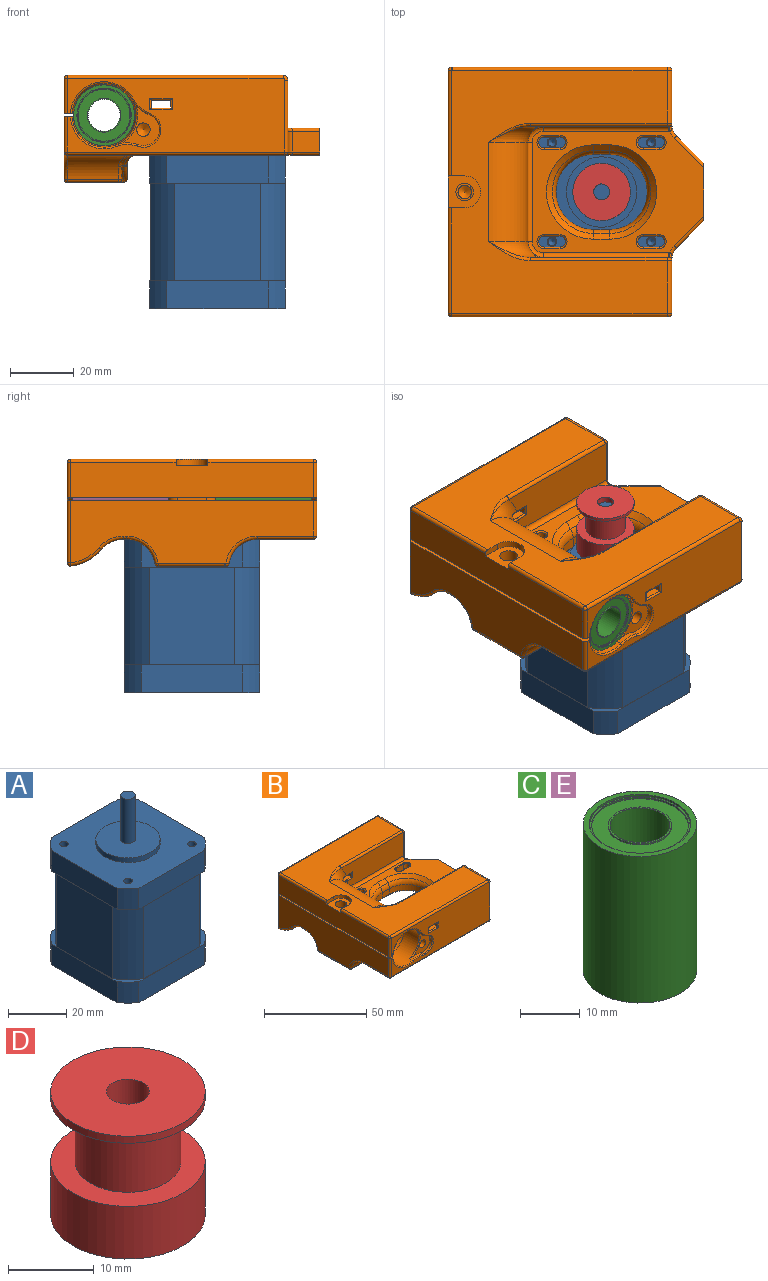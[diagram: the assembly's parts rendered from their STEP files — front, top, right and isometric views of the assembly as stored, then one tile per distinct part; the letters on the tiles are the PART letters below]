
ASSEMBLY  parts=5 mates=1
PART A: 48 faces, bbox 42.4x42.4x68.5 mm
  f0: cylinder r=1.5mm len=6mm, axis (0,0,1), area 56.5mm2, adj f18,f26
  f1: cylinder r=1.25mm len=2.5mm, axis (0,0,1), area 11.8mm2, adj f2,f26
  f2: cone r=1.25mm half-angle=59deg, axis (0,0,1), area 5.7mm2, adj f1
  f3: cylinder r=1.5mm len=6mm, axis (0,0,1), area 56.5mm2, adj f18,f25
  f4: cylinder r=1.25mm len=2.5mm, axis (0,0,1), area 11.8mm2, adj f5,f25
  f5: cone r=1.25mm half-angle=59deg, axis (0,0,1), area 5.7mm2, adj f4
  f6: cylinder r=1.5mm len=6mm, axis (0,0,1), area 56.5mm2, adj f18,f24
  f7: cylinder r=1.25mm len=2.5mm, axis (0,0,1), area 11.8mm2, adj f8,f24
  f8: cone r=1.25mm half-angle=59deg, axis (0,0,1), area 5.7mm2, adj f7
  f9: cylinder r=1.5mm len=6mm, axis (0,0,1), area 56.5mm2, adj f18,f23
  f10: cylinder r=1.25mm len=2.5mm, axis (0,0,1), area 11.8mm2, adj f11,f23
  f11: cone r=1.25mm half-angle=59deg, axis (0,0,1), area 5.7mm2, adj f10
  f12: cylinder r=11mm len=22mm, axis (0,0,-1), area 138.2mm2, adj f13,f18
  f13: plane 22x22mm, normal (0,0,1), area 360.5mm2, adj f12,f46
  f14: plane 31.78x8.75mm, normal (1,0,0), area 278mm2, adj f18,f19,f20,f28
  f15: plane 31.78x8.75mm, normal (0,-1,0), area 278mm2, adj f18,f19,f21,f28
  f16: plane 31.78x8.75mm, normal (-1,0,0), area 278mm2, adj f18,f21,f22,f28
  f17: plane 31.78x8.75mm, normal (0,1,0), area 278mm2, adj f18,f20,f22,f28
  f18: plane 42.42x42.42mm, normal (0,0,1), area 1339.6mm2, adj f0,f3,f6,f9,f12,f14,f15,f16
  f19: cylinder r=26.5mm len=8.75mm, axis (0,0,-1), area 66.1mm2, adj f14,f15,f18,f28
  f20: cylinder r=26.5mm len=8.75mm, axis (0,0,-1), area 66.1mm2, adj f14,f17,f18,f28
  f21: cylinder r=26.5mm len=8.75mm, axis (0,0,-1), area 66.1mm2, adj f15,f16,f18,f28
  f22: cylinder r=26.5mm len=8.75mm, axis (0,0,-1), area 66.1mm2, adj f16,f17,f18,f28
  f23: plane 3x3mm, normal (0,0,1), area 2.2mm2, adj f9,f10
  f24: plane 3x3mm, normal (0,0,1), area 2.2mm2, adj f6,f7
  f25: plane 3x3mm, normal (0,0,1), area 2.2mm2, adj f3,f4
  f26: plane 3x3mm, normal (0,0,1), area 2.2mm2, adj f0,f1
  f27: plane 42.42x42.42mm, normal (0,0,1), area 67.2mm2, adj f29,f30,f31,f32,f33,f34,f35,f36
  f28: plane 42.42x42.42mm, normal (0,0,-1), area 67.2mm2, adj f14,f15,f16,f17,f19,f20,f21,f22
  f29: cylinder r=25mm len=30.5mm, axis (0,0,1), area 335.5mm2, adj f27,f28,f30,f36
  f30: plane 30.5x26.79mm, normal (0,1,0), area 817.1mm2, adj f27,f28,f29,f31
  f31: cylinder r=25mm len=30.5mm, axis (0,0,1), area 335.5mm2, adj f27,f28,f30,f32
  f32: plane 30.5x26.79mm, normal (1,0,0), area 817.1mm2, adj f27,f28,f31,f33
  f33: cylinder r=25mm len=30.5mm, axis (0,0,1), area 335.5mm2, adj f27,f28,f32,f34
  f34: plane 30.5x26.79mm, normal (0,-1,0), area 817.1mm2, adj f27,f28,f33,f35
  f35: cylinder r=25mm len=30.5mm, axis (0,0,1), area 335.5mm2, adj f27,f28,f34,f36
  f36: plane 30.5x26.79mm, normal (-1,0,0), area 817.1mm2, adj f27,f28,f29,f35
  f37: plane 42.42x42.42mm, normal (0,0,-1), area 1748.1mm2, adj f38,f39,f40,f41,f42,f43,f44,f45
  f38: cylinder r=26.5mm len=8.75mm, axis (0,0,-1), area 66.1mm2, adj f27,f37,f44,f45
  f39: cylinder r=26.5mm len=8.75mm, axis (0,0,-1), area 66.1mm2, adj f27,f37,f43,f44
  f40: cylinder r=26.5mm len=8.75mm, axis (0,0,-1), area 66.1mm2, adj f27,f37,f42,f43
  f41: cylinder r=26.5mm len=8.75mm, axis (0,0,-1), area 66.1mm2, adj f27,f37,f42,f45
  f42: plane 31.78x8.75mm, normal (0,1,0), area 278mm2, adj f27,f37,f40,f41
  f43: plane 31.78x8.75mm, normal (-1,0,0), area 278mm2, adj f27,f37,f39,f40
  f44: plane 31.78x8.75mm, normal (0,-1,0), area 278mm2, adj f27,f37,f38,f39
  f45: plane 31.78x8.75mm, normal (1,0,0), area 278mm2, adj f27,f37,f38,f41
  f46: cylinder r=2.5mm len=18.5mm, axis (0,0,-1), area 290.6mm2, adj f13,f47
  f47: plane 5x5mm, normal (0,0,1), area 19.6mm2, adj f46
PART B: 337 faces, bbox 81.6x78.8x45.8 mm
  f0: cylinder r=1mm len=33mm, axis (0,1,0), area 51.8mm2, adj f4,f6,f161,f329
  f1: cylinder r=5mm len=10mm, axis (0,0,1), area 31.4mm2, adj f4,f325,f329,f330
  f2: plane 78.05x7.08mm, normal (0,0,-1), area 242.1mm2, adj f3,f6,f7,f8,f9,f10,f11,f12
  f3: cylinder r=5.5mm len=11mm, axis (0,1,0), area 289.9mm2, adj f2,f21,f22,f122,f324,f326,f328
  f4: plane 76.85x68.35mm, normal (0,0,1), area 2698.2mm2, adj f0,f1,f5,f105,f134,f135,f155,f164
  f5: cylinder r=1mm len=33mm, axis (0,1,0), area 51.8mm2, adj f4,f6,f167,f330
  f6: plane 76x11mm, normal (-1,0,0), area 826mm2, adj f0,f2,f5,f23,f24,f325,f329,f330
  f7: cylinder r=10mm len=20mm, axis (0,-1,0), area 697mm2, adj f2,f17,f25,f204,f205,f208,f306,f307
  f8: cylinder r=10mm len=20mm, axis (0,-1,0), area 704.4mm2, adj f2,f20,f26,f206,f207,f213,f309,f324
  f9: cylinder r=10mm len=20mm, axis (0,-1,0), area 738.3mm2, adj f2,f13,f19,f324
  f10: cylinder r=10mm len=20mm, axis (0,-1,0), area 730.9mm2, adj f2,f14,f18,f324
  f11: plane 68x31.41mm, normal (0,1,0), area 1163mm2, adj f2,f24,f25,f159,f160,f164,f166,f169
  f12: plane 68x23mm, normal (0,-1,0), area 1106.3mm2, adj f2,f23,f26,f144,f145,f150,f155,f156
  f13: plane 20x19.99mm, normal (0,-1,0), area 85.7mm2, adj f2,f9,f22,f324
  f14: plane 20x19.99mm, normal (0,1,0), area 85.7mm2, adj f2,f10,f21,f324
  f15: cylinder r=9.6mm len=19.2mm, axis (0,1,0), area 189.8mm2, adj f2,f19,f20,f324
  f16: cylinder r=9.5mm len=19mm, axis (0,-1,0), area 176.1mm2, adj f2,f17,f18,f324
  f17: torus R=5mm, axis (0,-1,0), area 137mm2, adj f2,f7,f16,f324
  f18: torus R=5mm, axis (0,1,0), area 137mm2, adj f2,f10,f16,f324
  f19: torus R=5mm, axis (0,-1,0), area 122.8mm2, adj f2,f9,f15,f324
  f20: torus R=5mm, axis (0,1,0), area 122.8mm2, adj f2,f8,f15,f324
  f21: torus R=8.5mm, axis (0,-1,0), area 188.9mm2, adj f2,f3,f14,f122,f324
  f22: torus R=8.5mm, axis (0,-1,0), area 184.3mm2, adj f2,f3,f13,f119,f120,f121,f324
  f23: cylinder r=1mm len=11mm, axis (0,0,-1), area 17.3mm2, adj f2,f6,f12,f161
  f24: cylinder r=1mm len=11mm, axis (0,0,1), area 17.3mm2, adj f2,f6,f11,f167
  f25: torus R=10.5mm, axis (0,1,0), area 15.1mm2, adj f7,f11,f210,f324
  f26: torus R=10.5mm, axis (0,1,0), area 20.8mm2, adj f2,f8,f12,f215
  f27: plane 79x76mm, normal (0,0,-1), area 3130.6mm2, adj f39,f113,f114,f115,f117,f118,f136,f137
  f28: plane 13.7x1mm, normal (1,0,0), area 13.7mm2, adj f96,f98,f99,f312
  f29: plane 13.7x1mm, normal (1,0,0), area 13.7mm2, adj f96,f97,f98,f310
  f30: plane 11.66x5.5mm, normal (1,0,0), area 45.6mm2, adj f31,f33,f107,f108,f109,f110,f217,f331
  f31: plane 13.7x6.1mm, normal (0,0,1), area 83.6mm2, adj f30,f32,f110,f219
  f32: plane 11.66x5.5mm, normal (-1,0,0), area 45.6mm2, adj f31,f33,f107,f108,f109,f110,f218,f332
  f33: plane 13.7x6.1mm, normal (0,0,-1), area 83.6mm2, adj f30,f32,f108,f216
  f34: plane 18.16x6mm, normal (0,0,1), area 84.3mm2, adj f36,f63,f260,f261,f274,f282
  f35: plane 17.81x6mm, normal (0,0,-1), area 105.2mm2, adj f36,f63,f84,f256,f257,f285
  f36: plane 18.42x2.63mm, normal (1,0,0), area 45.6mm2, adj f34,f35,f256,f258,f260,f283
  f37: plane 22.5x16.93mm, normal (1,0,0), area 255.2mm2, adj f104,f133,f134,f138,f144,f188,f189
  f38: plane 8.54x8.54mm, normal (0.71,-0.71,0), area 78.5mm2, adj f39,f104,f136,f185
  f39: plane 18.42x8.92mm, normal (1,0,0), area 56.2mm2, adj f27,f38,f40,f102,f136,f149,f177,f185
  f40: plane 8.54x8.54mm, normal (0.71,0.71,0), area 78.5mm2, adj f39,f103,f149,f177
  f41: plane 22.5x16.93mm, normal (1,0,0), area 255.2mm2, adj f103,f132,f135,f158,f159,f179,f182
  f42: plane 5x3.34mm, normal (0,1,0), area 16.7mm2, adj f52,f53,f237,f303
  f43: plane 5x3.34mm, normal (0,-1,0), area 16.7mm2, adj f52,f53,f238,f304
  f44: plane 7.5x5mm, normal (0,-1,0), area 37.5mm2, adj f54,f55,f225,f243
  f45: plane 7.5x5mm, normal (0,1,0), area 37.5mm2, adj f54,f55,f226,f240
  f46: plane 7.5x5mm, normal (0,-1,0), area 37.5mm2, adj f56,f57,f221,f247
  f47: plane 7.5x5mm, normal (0,1,0), area 37.5mm2, adj f56,f57,f222,f244
  f48: cylinder r=1.7mm len=7.5mm, axis (0,0,-1), area 40.1mm2, adj f49,f51,f232,f253
  f49: plane 7.5x5mm, normal (0,1,0), area 37.5mm2, adj f48,f50,f233,f252
  f50: cylinder r=1.7mm len=7.5mm, axis (0,0,-1), area 40.1mm2, adj f49,f51,f235,f254
  f51: plane 7.5x5mm, normal (0,-1,0), area 37.5mm2, adj f48,f50,f234,f255
  f52: cylinder r=11.75mm len=23.5mm, axis (0,0,-1), area 123.4mm2, adj f42,f43,f239,f302
  f53: cylinder r=11.75mm len=23.5mm, axis (0,0,-1), area 123.4mm2, adj f42,f43,f236,f305
  f54: cylinder r=1.7mm len=7.5mm, axis (0,0,-1), area 40.1mm2, adj f44,f45,f224,f242
  f55: cylinder r=1.7mm len=7.5mm, axis (0,0,-1), area 40.1mm2, adj f44,f45,f227,f241
  f56: cylinder r=1.7mm len=7.5mm, axis (0,0,-1), area 40.1mm2, adj f46,f47,f220,f246
  f57: cylinder r=1.7mm len=7.5mm, axis (0,0,-1), area 40.1mm2, adj f46,f47,f223,f245
  f58: cylinder r=1.7mm len=7.5mm, axis (0,0,-1), area 40.1mm2, adj f59,f61,f228,f249
  f59: plane 7.5x5mm, normal (0,1,0), area 37.5mm2, adj f58,f60,f229,f248
  f60: cylinder r=1.7mm len=7.5mm, axis (0,0,-1), area 40.1mm2, adj f59,f61,f231,f250
  f61: plane 7.5x5mm, normal (0,-1,0), area 37.5mm2, adj f58,f60,f230,f251
  f62: plane 18.42x2.63mm, normal (1,0,0), area 45.6mm2, adj f78,f79,f262,f264,f266,f286
  f63: plane 17.5x2.5mm, normal (-1,0,0), area 43.8mm2, adj f34,f35,f259,f284
  f64: cylinder r=5.15mm len=33mm, axis (1,0,0), area 1040.9mm2, adj f67,f76,f132,f290
  f65: cylinder r=5.15mm len=33mm, axis (1,0,0), area 1040.9mm2, adj f68,f72,f133,f294
  f66: plane 76x19.5mm, normal (-1,0,0), area 1125.4mm2, adj f141,f146,f152,f156,f162,f165,f168,f170
  f67: plane 10.3x10.3mm, normal (1,0,0), area 83.3mm2, adj f64
  f68: plane 10.3x10.3mm, normal (1,0,0), area 83.3mm2, adj f65
  f69: cylinder r=5mm len=10mm, axis (0,0,-1), area 125.7mm2, adj f296,f297
  f70: plane 9x9mm, normal (0,0,-1), area 42.4mm2, adj f295,f296
  f71: cylinder r=2.1mm len=4.83mm, axis (0,0,-1), area 59.6mm2, adj f294,f295
  f72: cone r=0mm half-angle=59deg, axis (0,0,-1), area 7.5mm2, adj f65
  f73: cylinder r=5mm len=10mm, axis (0,0,-1), area 125.7mm2, adj f292,f293
  f74: plane 9x9mm, normal (0,0,-1), area 42.4mm2, adj f291,f292
  f75: cylinder r=2.1mm len=4.83mm, axis (0,0,-1), area 59.6mm2, adj f290,f291
  f76: cone r=0mm half-angle=59deg, axis (0,0,-1), area 7.5mm2, adj f64
  f77: plane 17.5x2.5mm, normal (-1,0,0), area 43.8mm2, adj f78,f79,f265,f289
  f78: plane 18.16x6mm, normal (0,0,1), area 84.3mm2, adj f62,f77,f262,f263,f278,f288
  f79: plane 17.81x6mm, normal (0,0,-1), area 105.2mm2, adj f62,f77,f80,f266,f267,f287
  f80: cone r=0mm half-angle=59deg, axis (0,0,-1), area 0mm2, adj f79
  f81: cylinder r=2.1mm len=8.25mm, axis (0,0,-1), area 108.9mm2, adj f278,f279
  f82: plane 9x9mm, normal (0,0,-1), area 42.4mm2, adj f279,f280
  f83: cylinder r=5mm len=10mm, axis (0,0,-1), area 141.4mm2, adj f280,f281
  f84: cone r=0mm half-angle=59deg, axis (0,0,-1), area 0mm2, adj f35
  f85: cylinder r=2.1mm len=8.25mm, axis (0,0,-1), area 108.9mm2, adj f274,f275
  f86: plane 9x9mm, normal (0,0,-1), area 42.4mm2, adj f275,f276
  f87: cylinder r=5mm len=10mm, axis (0,0,-1), area 141.4mm2, adj f276,f277
  f88: plane 12.42x11.48mm, normal (0,-1,0), area 58.3mm2, adj f89,f91,f206,f207,f309
  f89: cylinder r=5mm len=9.68mm, axis (0,-1,0), area 23.4mm2, adj f88,f206,f207,f214
  f90: cone r=0mm half-angle=59deg, axis (0,-1,0), area 16.2mm2, adj f91
  f91: cylinder r=2.1mm len=15mm, axis (0,-1,0), area 197.9mm2, adj f88,f90
  f92: plane 12.42x11.48mm, normal (0,1,0), area 50.9mm2, adj f93,f204,f205,f273,f306,f308
  f93: cylinder r=5mm len=9.68mm, axis (0,1,0), area 23.4mm2, adj f92,f204,f205,f211
  f94: cone r=0mm half-angle=59deg, axis (0,1,0), area 12.6mm2, adj f272
  f95: cylinder r=2.1mm len=14.22mm, axis (0,1,0), area 187.6mm2, adj f272,f273
  f96: plane 6.1x5.5mm, normal (0,1,0), area 33.6mm2, adj f28,f29,f97,f99,f268,f311
  f97: plane 13.7x6.1mm, normal (0,0,1), area 83.6mm2, adj f29,f96,f98,f270
  f98: plane 6.1x5.5mm, normal (0,-1,0), area 33.6mm2, adj f28,f29,f97,f99,f271,f313
  f99: plane 13.7x6.1mm, normal (0,0,-1), area 83.6mm2, adj f28,f96,f98,f269
  f100: plane 43.31x14mm, normal (0,1,0), area 547.1mm2, adj f130,f184,f186,f189,f196,f263,f265,f267
  f101: plane 43.31x14mm, normal (0,-1,0), area 547.1mm2, adj f131,f178,f181,f182,f200,f257,f259,f261
  f102: plane 53.73x38.05mm, normal (0,0,1), area 927.3mm2, adj f39,f177,f180,f185,f187,f195,f196,f197
  f103: cylinder r=5mm len=6.5mm, axis (0,0,1), area 25.5mm2, adj f40,f41,f154,f180
  f104: cylinder r=5mm len=6.5mm, axis (0,0,1), area 25.5mm2, adj f37,f38,f137,f187
  f105: cylinder r=12.5mm len=31mm, axis (0,-1,0), area 678.3mm2, adj f4,f130,f131,f198
  f106: plane 8.55x4.41mm, normal (1,0,0), area 24.3mm2, adj f118,f125,f172
  f107: plane 14.25x6.41mm, normal (0,0,-1), area 87.3mm2, adj f30,f32,f108,f333,f335,f336
  f108: plane 13.7x1.2mm, normal (0,1,0), area 16.4mm2, adj f30,f32,f33,f107
  f109: plane 13.7x1.76mm, normal (0,0,1), area 24.1mm2, adj f30,f32,f110,f332
  f110: plane 13.7x1.2mm, normal (0,1,0), area 16.4mm2, adj f30,f31,f32,f109
  f111: plane 21.2x16mm, normal (0,0,-1), area 291.5mm2, adj f142,f143,f152,f153,f190,f191,f192
  f112: plane 24.97x4.5mm, normal (1,0,0), area 101.9mm2, adj f117,f126,f128,f143
  f113: cylinder r=9mm len=20mm, axis (-1,0,0), area 221.2mm2, adj f27,f128,f129,f153,f162
  f114: cylinder r=9mm len=20mm, axis (-1,0,0), area 221.2mm2, adj f27,f126,f127,f141,f142
  f115: cylinder r=9mm len=21.7mm, axis (1,0,0), area 106.5mm2, adj f27,f116,f123,f168,f333,f335,f336
  f116: cylinder r=15mm len=17.73mm, axis (1,0,0), area 155.6mm2, adj f115,f124,f125,f171,f175,f331,f332,f334
  f117: cylinder r=3mm len=40.97mm, axis (0,1,0), area 155.4mm2, adj f27,f112,f127,f129
  f118: cylinder r=3mm len=16.59mm, axis (0,1,0), area 57.1mm2, adj f27,f106,f123,f124,f169
  f119: cylinder r=1.25mm len=14.61mm, axis (0,0,-1), area 109.6mm2, adj f22,f191
  f120: cylinder r=1.25mm len=19mm, axis (0,0,-1), area 149.2mm2, adj f22,f121,f192
  f121: plane 2.5x2.5mm, normal (0,0,-1), area 4.9mm2, adj f22,f120
  f122: cylinder r=1.25mm len=17.06mm, axis (0,0,-1), area 126mm2, adj f3,f21,f190
  f123: bspline ~8.31x4.01mm, area 4.3mm2, adj f115,f118,f124
  f124: bspline ~2.81x2.65mm, area 0.9mm2, adj f116,f118,f123,f125
  f125: torus R=14mm, axis (1,0,0), area 16.1mm2, adj f106,f116,f124,f174
  f126: torus R=10mm, axis (1,0,0), area 7.3mm2, adj f112,f114,f127,f139
  f127: bspline ~8.57x4.36mm, area 4.8mm2, adj f114,f117,f126
  f128: torus R=10mm, axis (1,0,0), area 7.3mm2, adj f112,f113,f129,f148
  f129: bspline ~8.57x4.36mm, area 4.8mm2, adj f113,f117,f128
  f130: torus R=17.5mm, axis (0,-1,0), area 134.5mm2, adj f100,f105,f183,f197,f262,f264,f266
  f131: torus R=17.5mm, axis (0,-1,0), area 134.5mm2, adj f101,f105,f176,f199,f256,f258,f260
  f132: cone r=5.15mm half-angle=45deg, axis (1,0,0), area 50.2mm2, adj f41,f64
  f133: cone r=5.15mm half-angle=45deg, axis (1,0,0), area 50.2mm2, adj f37,f65
  f134: cylinder r=1.5mm len=16.5mm, axis (0,-1,0), area 38.9mm2, adj f4,f37,f150,f186
  f135: cylinder r=1.5mm len=16.5mm, axis (0,-1,0), area 38.9mm2, adj f4,f41,f160,f181
  f136: cylinder r=1mm len=9.95mm, axis (0.71,0.71,0), area 19.7mm2, adj f27,f38,f39,f137
  f137: torus R=6mm, axis (0,0,1), area 6.6mm2, adj f27,f104,f136,f138
  f138: cylinder r=1mm len=16.93mm, axis (0,1,0), area 26.6mm2, adj f27,f37,f137,f140
  f139: sphere r=1mm, area 0.9mm2, adj f126,f142,f143
  f140: sphere r=1mm, area 1.6mm2, adj f138,f144,f145
  f141: torus R=10mm, axis (1,0,0), area 20.9mm2, adj f66,f114,f146,f147
  f142: cylinder r=1mm len=16mm, axis (-1,0,0), area 22.7mm2, adj f111,f114,f139,f147
  f143: cylinder r=1mm len=21.2mm, axis (0,1,0), area 33.3mm2, adj f111,f112,f139,f148
  f144: cylinder r=1mm len=22.5mm, axis (0,0,1), area 35.3mm2, adj f12,f37,f140,f150
  f145: cylinder r=1mm len=68mm, axis (1,0,0), area 106.8mm2, adj f12,f27,f140,f151
  f146: cylinder r=1mm len=17.51mm, axis (0,-1,0), area 27.5mm2, adj f27,f66,f141,f151
  f147: sphere r=1mm, area 2mm2, adj f141,f142,f152
  f148: sphere r=1mm, area 1mm2, adj f128,f143,f153
  f149: cylinder r=1mm len=9.95mm, axis (-0.71,0.71,0), area 19.7mm2, adj f27,f39,f40,f154
  f150: torus R=0.5mm, axis (0,1,0), area 2.8mm2, adj f12,f134,f144,f155
  f151: sphere r=1mm, area 1.6mm2, adj f145,f146,f156
  f152: cylinder r=1mm len=21.2mm, axis (0,1,0), area 33.3mm2, adj f66,f111,f147,f157
  f153: cylinder r=1mm len=16mm, axis (-1,0,0), area 22.7mm2, adj f111,f113,f148,f157
  f154: torus R=6mm, axis (0,0,1), area 6.6mm2, adj f27,f103,f149,f158
  f155: cylinder r=1mm len=67.5mm, axis (-1,0,0), area 106mm2, adj f4,f12,f150,f161
  f156: cylinder r=1mm len=11mm, axis (0,0,-1), area 17.3mm2, adj f12,f66,f151,f324
  f157: sphere r=1mm, area 1.9mm2, adj f152,f153,f162
  f158: cylinder r=1mm len=16.93mm, axis (0,1,0), area 26.6mm2, adj f27,f41,f154,f163
  f159: cylinder r=1mm len=22.5mm, axis (0,0,-1), area 35.3mm2, adj f11,f41,f160,f163
  f160: torus R=0.5mm, axis (0,1,0), area 2.8mm2, adj f11,f135,f159,f164
  f161: sphere r=1mm, area 1.6mm2, adj f0,f23,f155
  f162: torus R=10mm, axis (1,0,0), area 20.9mm2, adj f66,f113,f157,f165
  f163: sphere r=1mm, area 1mm2, adj f158,f159,f166
  f164: cylinder r=1mm len=67.5mm, axis (1,0,0), area 106mm2, adj f4,f11,f160,f167
  f165: cylinder r=1mm len=1mm, axis (0,-1,0), area 1.5mm2, adj f27,f66,f162,f168
  f166: cylinder r=1mm len=46.3mm, axis (-1,0,0), area 72.7mm2, adj f11,f27,f163,f169
  f167: sphere r=1mm, area 2.1mm2, adj f5,f24,f164
  f168: torus R=10mm, axis (1,0,0), area 12.8mm2, adj f66,f115,f165,f171
  f169: torus R=4mm, axis (0,1,0), area 8.3mm2, adj f11,f118,f166,f172
  f170: cylinder r=1mm len=19.41mm, axis (0,0,1), area 30.5mm2, adj f11,f66,f173,f324
  f171: torus R=14mm, axis (1,0,0), area 17.1mm2, adj f66,f116,f168,f173
  f172: cylinder r=1mm len=4.41mm, axis (0,0,-1), area 6.9mm2, adj f11,f106,f169,f174
  f173: sphere r=1mm, area 1.7mm2, adj f170,f171,f175
  f174: sphere r=1mm, area 2.2mm2, adj f125,f172,f175
  f175: cylinder r=1mm len=17.7mm, axis (1,0,0), area 30mm2, adj f11,f116,f173,f174
  f176: bspline ~14.21x6mm, area 7.9mm2, adj f4,f131,f178
  f177: cylinder r=1mm len=9.95mm, axis (0.71,-0.71,0), area 19.7mm2, adj f39,f40,f102,f180
  f178: cylinder r=1mm len=42.81mm, axis (1,0,0), area 67.2mm2, adj f4,f101,f176,f181
  f179: cylinder r=1mm len=0.43mm, axis (0,1,0), area 0mm2, adj f41,f180,f203
  f180: torus R=6mm, axis (0,0,1), area 4.6mm2, adj f102,f103,f177,f179,f202
  f181: torus R=0.5mm, axis (0,-1,0), area 2.8mm2, adj f101,f135,f178,f182
  f182: cylinder r=1mm len=16mm, axis (0,0,1), area 22.5mm2, adj f41,f101,f181,f201,f202,f203
  f183: bspline ~14.21x6mm, area 7.8mm2, adj f4,f130,f184
  f184: cylinder r=1mm len=42.81mm, axis (-1,0,0), area 67.2mm2, adj f4,f100,f183,f186
  f185: cylinder r=1mm len=9.95mm, axis (-0.71,-0.71,0), area 19.7mm2, adj f38,f39,f102,f187
  f186: torus R=0.5mm, axis (0,-1,0), area 2.8mm2, adj f100,f134,f184,f189
  f187: torus R=6mm, axis (0,0,1), area 4.6mm2, adj f102,f104,f185,f188,f194
  f188: cylinder r=1mm len=0.43mm, axis (0,1,0), area 0mm2, adj f37,f187,f193
  f189: cylinder r=1mm len=16mm, axis (0,0,1), area 22.5mm2, adj f37,f100,f186,f193,f194,f195
  f190: torus R=2.25mm, axis (0,0,1), area 15.9mm2, adj f111,f122
  f191: torus R=2.25mm, axis (0,0,1), area 15.9mm2, adj f111,f119
  f192: torus R=2.25mm, axis (0,0,1), area 15.9mm2, adj f111,f120
  f193: bspline ~0.57x0.57mm, area 0.1mm2, adj f188,f189,f194
  f194: bspline ~2.35x2.33mm, area 2.8mm2, adj f187,f189,f193,f195
  f195: torus R=2.5mm, axis (0,0,1), area 0.5mm2, adj f102,f189,f194,f196
  f196: cylinder r=1.5mm len=39.18mm, axis (1,0,0), area 92.3mm2, adj f100,f102,f195,f197
  f197: bspline ~6.47x6.18mm, area 17.9mm2, adj f102,f130,f196,f198
  f198: cylinder r=1.5mm len=31mm, axis (0,-1,0), area 81.4mm2, adj f102,f105,f197,f199
  f199: bspline ~6.47x6.18mm, area 17.9mm2, adj f102,f131,f198,f200
  f200: cylinder r=1.5mm len=39.18mm, axis (-1,0,0), area 92.3mm2, adj f101,f102,f199,f201
  f201: torus R=2.5mm, axis (0,0,1), area 0.5mm2, adj f102,f182,f200,f202
  f202: bspline ~2.36x2.34mm, area 2.8mm2, adj f180,f182,f201,f203
  f203: bspline ~0.57x0.57mm, area 0.1mm2, adj f179,f182,f202
  f204: cylinder r=10mm len=5.27mm, axis (0,1,0), area 11.3mm2, adj f7,f92,f93,f209,f306
  f205: cylinder r=10mm len=6.99mm, axis (0,-1,0), area 11.3mm2, adj f7,f92,f93,f210,f308
  f206: cylinder r=10mm len=5.27mm, axis (0,1,0), area 11.3mm2, adj f8,f88,f89,f215,f309
  f207: cylinder r=10mm len=6.99mm, axis (0,-1,0), area 11.3mm2, adj f8,f88,f89,f212,f309
  f208: torus R=10.5mm, axis (0,1,0), area 20.8mm2, adj f2,f7,f11,f209
  f209: torus R=9.5mm, axis (0,1,0), area 5.5mm2, adj f11,f204,f208,f211
  f210: torus R=9.5mm, axis (0,1,0), area 5.5mm2, adj f11,f25,f205,f211
  f211: torus R=5.5mm, axis (0,1,0), area 12.7mm2, adj f11,f93,f209,f210
  f212: torus R=9.5mm, axis (0,1,0), area 5.5mm2, adj f12,f207,f213,f214
  f213: torus R=10.5mm, axis (0,1,0), area 15.1mm2, adj f8,f12,f212,f324
  f214: torus R=5.5mm, axis (0,1,0), area 12.7mm2, adj f12,f89,f212,f215
  f215: torus R=9.5mm, axis (0,1,0), area 5.5mm2, adj f12,f26,f206,f214
  f216: cylinder r=0.5mm len=14.7mm, axis (-1,0,0), area 11.2mm2, adj f11,f33,f217,f218
  f217: cylinder r=0.5mm len=6.5mm, axis (0,0,-1), area 4.7mm2, adj f11,f30,f216,f219
  f218: cylinder r=0.5mm len=6.5mm, axis (0,0,1), area 4.7mm2, adj f11,f32,f216,f219
  f219: cylinder r=0.5mm len=14.7mm, axis (1,0,0), area 11.2mm2, adj f11,f31,f217,f218
  f220: torus R=2.2mm, axis (0,0,1), area 4.6mm2, adj f56,f102,f221,f222
  f221: cylinder r=0.5mm len=5mm, axis (-1,0,0), area 3.9mm2, adj f46,f102,f220,f223
  f222: cylinder r=0.5mm len=5mm, axis (1,0,0), area 3.9mm2, adj f47,f102,f220,f223
  f223: torus R=2.2mm, axis (0,0,1), area 4.6mm2, adj f57,f102,f221,f222
  f224: torus R=2.2mm, axis (0,0,1), area 4.6mm2, adj f54,f102,f225,f226
  f225: cylinder r=0.5mm len=5mm, axis (-1,0,0), area 3.9mm2, adj f44,f102,f224,f227
  f226: cylinder r=0.5mm len=5mm, axis (1,0,0), area 3.9mm2, adj f45,f102,f224,f227
  f227: torus R=2.2mm, axis (0,0,1), area 4.6mm2, adj f55,f102,f225,f226
  f228: torus R=2.2mm, axis (0,0,1), area 4.6mm2, adj f58,f102,f229,f230
  f229: cylinder r=0.5mm len=5mm, axis (1,0,0), area 3.9mm2, adj f59,f102,f228,f231
  f230: cylinder r=0.5mm len=5mm, axis (-1,0,0), area 3.9mm2, adj f61,f102,f228,f231
  f231: torus R=2.2mm, axis (0,0,1), area 4.6mm2, adj f60,f102,f229,f230
  f232: torus R=2.2mm, axis (0,0,1), area 4.6mm2, adj f48,f102,f233,f234
  f233: cylinder r=0.5mm len=5mm, axis (1,0,0), area 3.9mm2, adj f49,f102,f232,f235
  f234: cylinder r=0.5mm len=5mm, axis (-1,0,0), area 3.9mm2, adj f51,f102,f232,f235
  f235: torus R=2.2mm, axis (0,0,1), area 4.6mm2, adj f50,f102,f233,f234
  f236: torus R=12.25mm, axis (0,0,1), area 29.4mm2, adj f27,f53,f237,f238
  f237: cylinder r=0.5mm len=5mm, axis (-1,0,0), area 3.9mm2, adj f27,f42,f236,f239
  f238: cylinder r=0.5mm len=5mm, axis (1,0,0), area 3.9mm2, adj f27,f43,f236,f239
  f239: torus R=12.25mm, axis (0,0,1), area 29.4mm2, adj f27,f52,f237,f238
  f240: cylinder r=0.5mm len=5mm, axis (-1,0,0), area 3.9mm2, adj f27,f45,f241,f242
  f241: torus R=2.2mm, axis (0,0,1), area 4.6mm2, adj f27,f55,f240,f243
  f242: torus R=2.2mm, axis (0,0,1), area 4.6mm2, adj f27,f54,f240,f243
  f243: cylinder r=0.5mm len=5mm, axis (1,0,0), area 3.9mm2, adj f27,f44,f241,f242
  f244: cylinder r=0.5mm len=5mm, axis (-1,0,0), area 3.9mm2, adj f27,f47,f245,f246
  f245: torus R=2.2mm, axis (0,0,1), area 4.6mm2, adj f27,f57,f244,f247
  f246: torus R=2.2mm, axis (0,0,1), area 4.6mm2, adj f27,f56,f244,f247
  f247: cylinder r=0.5mm len=5mm, axis (1,0,0), area 3.9mm2, adj f27,f46,f245,f246
  f248: cylinder r=0.5mm len=5mm, axis (-1,0,0), area 3.9mm2, adj f27,f59,f249,f250
  f249: torus R=2.2mm, axis (0,0,1), area 4.6mm2, adj f27,f58,f248,f251
  f250: torus R=2.2mm, axis (0,0,1), area 4.6mm2, adj f27,f60,f248,f251
  f251: cylinder r=0.5mm len=5mm, axis (1,0,0), area 3.9mm2, adj f27,f61,f249,f250
  f252: cylinder r=0.5mm len=5mm, axis (-1,0,0), area 3.9mm2, adj f27,f49,f253,f254
  f253: torus R=2.2mm, axis (0,0,1), area 4.6mm2, adj f27,f48,f252,f255
  f254: torus R=2.2mm, axis (0,0,1), area 4.6mm2, adj f27,f50,f252,f255
  f255: cylinder r=0.5mm len=5mm, axis (1,0,0), area 3.9mm2, adj f27,f51,f253,f254
  f256: bspline ~4.58x1.46mm, area 1.7mm2, adj f35,f36,f131,f257,f258
  f257: cylinder r=0.5mm len=4.61mm, axis (-1,0,0), area 3.4mm2, adj f35,f101,f256,f259
  f258: bspline ~6.35x1.23mm, area 1.6mm2, adj f36,f131,f256,f260
  f259: cylinder r=0.5mm len=3.5mm, axis (0,0,1), area 2.4mm2, adj f63,f101,f257,f261
  f260: bspline ~4.71x1.61mm, area 2.2mm2, adj f34,f36,f131,f258,f261
  f261: cylinder r=0.5mm len=3.89mm, axis (1,0,0), area 2.9mm2, adj f34,f101,f259,f260
  f262: bspline ~4.71x1.61mm, area 2.2mm2, adj f62,f78,f130,f263,f264
  f263: cylinder r=0.5mm len=3.89mm, axis (-1,0,0), area 2.9mm2, adj f78,f100,f262,f265
  f264: bspline ~6.35x1.23mm, area 1.6mm2, adj f62,f130,f262,f266
  f265: cylinder r=0.5mm len=3.5mm, axis (0,0,-1), area 2.4mm2, adj f77,f100,f263,f267
  f266: bspline ~4.58x1.46mm, area 1.7mm2, adj f62,f79,f130,f264,f267
  f267: cylinder r=0.5mm len=4.61mm, axis (1,0,0), area 3.4mm2, adj f79,f100,f265,f266
  f268: cylinder r=0.5mm len=6.5mm, axis (0,0,1), area 4.7mm2, adj f39,f96,f269,f270
  f269: cylinder r=0.5mm len=14.7mm, axis (0,1,0), area 11.2mm2, adj f39,f99,f268,f271
  f270: cylinder r=0.5mm len=14.7mm, axis (0,-1,0), area 11.2mm2, adj f39,f97,f268,f271
  f271: cylinder r=0.5mm len=6.5mm, axis (0,0,-1), area 4.7mm2, adj f39,f98,f269,f270
  f272: torus R=1.6mm, axis (0,1,0), area 6.5mm2, adj f94,f95
  f273: torus R=2.6mm, axis (0,1,0), area 11.3mm2, adj f92,f95,f307
  f274: torus R=2.6mm, axis (0,0,-1), area 11.3mm2, adj f34,f85
  f275: torus R=2.6mm, axis (0,0,-1), area 11.3mm2, adj f85,f86
  f276: torus R=4.5mm, axis (0,0,-1), area 23.8mm2, adj f86,f87
  f277: torus R=5.5mm, axis (0,0,1), area 25.6mm2, adj f27,f87
  f278: torus R=2.6mm, axis (0,0,-1), area 11.3mm2, adj f78,f81
  f279: torus R=2.6mm, axis (0,0,-1), area 11.3mm2, adj f81,f82
  f280: torus R=4.5mm, axis (0,0,-1), area 23.8mm2, adj f82,f83
  f281: torus R=5.5mm, axis (0,0,1), area 25.6mm2, adj f27,f83
  f282: cylinder r=0.5mm len=7mm, axis (-1,0,0), area 5.1mm2, adj f11,f34,f283,f284
  f283: cylinder r=0.5mm len=3.5mm, axis (0,0,1), area 2.4mm2, adj f11,f36,f282,f285
  f284: cylinder r=0.5mm len=3.5mm, axis (0,0,-1), area 2.4mm2, adj f11,f63,f282,f285
  f285: cylinder r=0.5mm len=7mm, axis (1,0,0), area 5.1mm2, adj f11,f35,f283,f284
  f286: cylinder r=0.5mm len=3.5mm, axis (0,0,-1), area 2.4mm2, adj f12,f62,f287,f288
  f287: cylinder r=0.5mm len=7mm, axis (-1,0,0), area 5.1mm2, adj f12,f79,f286,f289
  f288: cylinder r=0.5mm len=7mm, axis (1,0,0), area 5.1mm2, adj f12,f78,f286,f289
  f289: cylinder r=0.5mm len=3.5mm, axis (0,0,1), area 2.4mm2, adj f12,f77,f287,f288
  f290: bspline ~5.2x4.74mm, area 9.5mm2, adj f64,f75
  f291: torus R=2.6mm, axis (0,0,-1), area 11.3mm2, adj f74,f75
  f292: torus R=4.5mm, axis (0,0,-1), area 23.8mm2, adj f73,f74
  f293: torus R=5.5mm, axis (0,0,1), area 25.6mm2, adj f27,f73
  f294: bspline ~5.2x4.74mm, area 9.5mm2, adj f65,f71
  f295: torus R=2.6mm, axis (0,0,-1), area 11.3mm2, adj f70,f71
  f296: torus R=4.5mm, axis (0,0,-1), area 23.8mm2, adj f69,f70
  f297: torus R=5.5mm, axis (0,0,1), area 25.6mm2, adj f27,f69
  f298: plane 5x1.83mm, normal (0,-0.71,0.71), area 12.9mm2, adj f102,f299,f300,f304
  f299: cone r=14.75mm half-angle=45deg, axis (0,0,1), area 112.4mm2, adj f102,f298,f301,f302
  f300: cone r=14.75mm half-angle=45deg, axis (0,0,1), area 112.4mm2, adj f102,f298,f301,f305
  f301: plane 5x1.83mm, normal (0,0.71,0.71), area 12.9mm2, adj f102,f299,f300,f303
  f302: torus R=15.75mm, axis (0,0,-1), area 119.9mm2, adj f52,f299,f303,f304
  f303: cylinder r=4mm len=5mm, axis (-1,0,0), area 15.7mm2, adj f42,f301,f302,f305
  f304: cylinder r=4mm len=5mm, axis (1,0,0), area 15.7mm2, adj f43,f298,f302,f305
  f305: torus R=15.75mm, axis (0,0,-1), area 119.9mm2, adj f53,f300,f303,f304
  f306: torus R=10.5mm, axis (0,1,0), area 5.8mm2, adj f7,f92,f204,f307
  f307: bspline ~0.73x0.68mm, area 0.2mm2, adj f7,f273,f306,f308
  f308: torus R=10.5mm, axis (0,1,0), area 5.8mm2, adj f7,f92,f205,f307
  f309: torus R=10.5mm, axis (0,-1,0), area 11.8mm2, adj f8,f88,f206,f207
  f310: bspline ~20.34x14.78mm, area 120.9mm2, adj f29,f311,f313,f317
  f311: bspline ~19.16x15.72mm, area 68.1mm2, adj f96,f310,f312,f316
  f312: bspline ~19.42x15.7mm, area 132.5mm2, adj f28,f311,f313,f315
  f313: bspline ~14.52x6.65mm, area 43.9mm2, adj f98,f310,f312,f314
  f314: extruded ~4.47x4.47mm, area 11.8mm2, adj f313,f315,f317,f320
  f315: extruded ~4.72x4.72mm, area 11.8mm2, adj f312,f314,f316,f321
  f316: extruded ~4.47x4.47mm, area 11.8mm2, adj f311,f315,f317,f318
  f317: extruded ~4.72x4.72mm, area 11.8mm2, adj f310,f314,f316,f319
  f318: bspline ~20.08x6.79mm, area 47.9mm2, adj f316,f319,f321,f322
  f319: bspline ~21.27x6.66mm, area 52.1mm2, adj f317,f318,f320,f322
  f320: bspline ~21.27x6.23mm, area 50.5mm2, adj f314,f319,f321,f322
  f321: bspline ~20.34x5.39mm, area 47.5mm2, adj f315,f318,f320,f322
  f322: bspline ~10.94x5.6mm, area 91.8mm2, adj f318,f319,f320,f321,f323
  f323: bspline ~5.65x5.56mm, area 18.2mm2, adj f27,f322
  f324: plane 78.05x7.08mm, normal (0,0,1), area 249.8mm2, adj f3,f7,f8,f9,f10,f11,f12,f13
  f325: plane 10.2x10mm, normal (0,0,1), area 67.5mm2, adj f1,f6,f328,f329,f330
  f326: cylinder r=2.1mm len=17mm, axis (0,0,1), area 222.9mm2, adj f3,f324,f327
  f327: cone r=0mm half-angle=59deg, axis (0,0,1), area 16.2mm2, adj f326
  f328: cylinder r=2.75mm len=10mm, axis (0,0,1), area 166.8mm2, adj f2,f3,f325
  f329: plane 5.2x2mm, normal (0,1,0), area 10.2mm2, adj f0,f1,f4,f6,f325
  f330: plane 5.2x2mm, normal (0,-1,0), area 10.2mm2, adj f1,f4,f5,f6,f325
  f331: torus R=14.5mm, axis (-1,0,0), area 2mm2, adj f30,f116,f332,f333
  f332: cylinder r=0.5mm len=14.7mm, axis (1,0,0), area 17.3mm2, adj f30,f32,f109,f116,f331,f334
  f333: torus R=9.5mm, axis (-1,0,0), area 2.3mm2, adj f30,f107,f115,f331,f335
  f334: torus R=14.5mm, axis (-1,0,0), area 2mm2, adj f32,f116,f332,f336
  f335: cylinder r=0.5mm len=14.7mm, axis (1,0,0), area 3.7mm2, adj f107,f115,f333,f336
  f336: torus R=9.5mm, axis (-1,0,0), area 2.3mm2, adj f32,f107,f115,f334,f335
PART C: 20 faces, bbox 19x19x30 mm
  f0: plane 19x19mm, normal (0,0,1), area 56.5mm2, adj f1,f19
  f1: cylinder r=9.5mm len=30mm, axis (0,0,-1), area 1790.7mm2, adj f0,f2
  f2: plane 19x19mm, normal (0,0,-1), area 56.5mm2, adj f1,f3
  f3: cylinder r=8.5mm len=17mm, axis (0,0,-1), area 32mm2, adj f2,f4
  f4: plane 17x17mm, normal (0,0,-1), area 5.3mm2, adj f3,f5
  f5: cylinder r=8.4mm len=16.8mm, axis (0,0,-1), area 15.8mm2, adj f4,f6
  f6: plane 16.8x16.8mm, normal (0,0,-1), area 15.6mm2, adj f5,f7
  f7: cylinder r=8.1mm len=16.2mm, axis (0,0,-1), area 15.3mm2, adj f6,f8
  f8: plane 16.2x16.2mm, normal (0,0,-1), area 117.9mm2, adj f7,f9
  f9: cylinder r=5.3mm len=10.6mm, axis (0,0,-1), area 10mm2, adj f8,f10
  f10: plane 10.6x10.6mm, normal (0,0,-1), area 9.7mm2, adj f9,f11
  f11: cylinder r=5mm len=29.4mm, axis (0,0,-1), area 923.6mm2, adj f10,f12
  f12: plane 10.6x10.6mm, normal (0,0,1), area 9.7mm2, adj f11,f13
  f13: cylinder r=5.3mm len=10.6mm, axis (0,0,-1), area 10mm2, adj f12,f14
  f14: plane 16.2x16.2mm, normal (0,0,1), area 117.9mm2, adj f13,f15
  f15: cylinder r=8.1mm len=16.2mm, axis (0,0,-1), area 15.3mm2, adj f14,f16
  f16: plane 16.8x16.8mm, normal (0,0,1), area 15.6mm2, adj f15,f17
  f17: cylinder r=8.4mm len=16.8mm, axis (0,0,-1), area 15.8mm2, adj f16,f18
  f18: plane 17x17mm, normal (0,0,1), area 5.3mm2, adj f17,f19
  f19: cylinder r=8.5mm len=17mm, axis (0,0,-1), area 32mm2, adj f0,f18
PART D: 8 faces, bbox 18x18x17.5 mm
  f0: cylinder r=9mm len=18mm, axis (0,0,-1), area 424.1mm2, adj f1,f7
  f1: plane 18x18mm, normal (0,0,-1), area 234.8mm2, adj f0,f2
  f2: cylinder r=2.5mm len=17.5mm, axis (0,0,-1), area 274.9mm2, adj f1,f3
  f3: plane 18x18mm, normal (0,0,1), area 234.8mm2, adj f2,f4
  f4: cylinder r=9mm len=18mm, axis (0,0,-1), area 56.5mm2, adj f3,f5
  f5: plane 18x18mm, normal (0,0,-1), area 135.6mm2, adj f4,f6
  f6: cylinder r=6.15mm len=12.3mm, axis (0,0,-1), area 347.8mm2, adj f5,f7
  f7: plane 18x18mm, normal (0,0,1), area 135.6mm2, adj f0,f6
PART E: same geometry as C
PLACE A t=(-2.5,0,0)mm
PLACE B t=(-15.5,0,12.5)mm
PLACE C rot(axis=(1,0,0),90deg) t=(-38,-22.35,12.5)mm
PLACE D t=(-2.5,0,4.75)mm
PLACE E rot(axis=(1,0,0),90deg) t=(-38,22.35,12.5)mm
MATE fastened A.f12 <-> B.f27  axis (0,0,1) through (-2.5,0,0)mm
